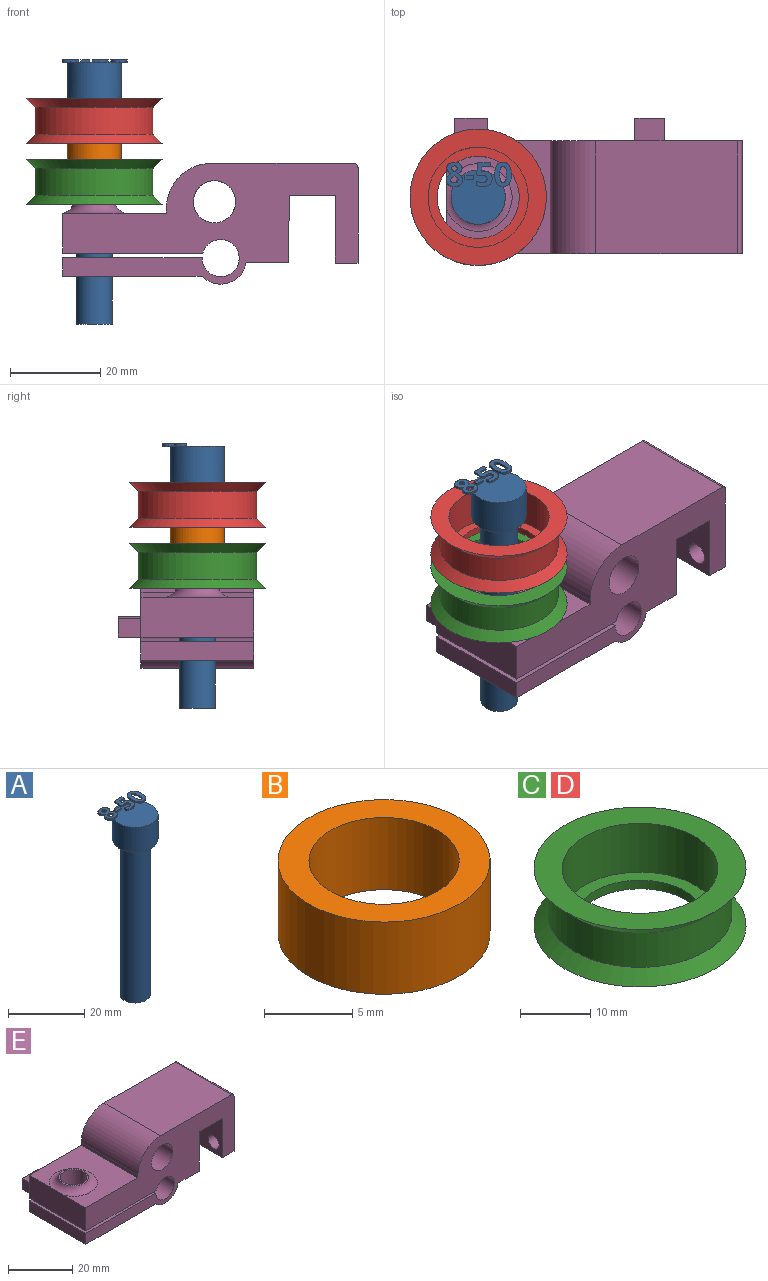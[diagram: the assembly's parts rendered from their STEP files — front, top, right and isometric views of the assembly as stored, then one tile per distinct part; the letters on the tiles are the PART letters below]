
ASSEMBLY  parts=5 mates=4
PART A: 86 faces, bbox 14.5x13.7x58.5 mm
  f0: plane 12x12mm, normal (0,0,1), area 99.4mm2, adj f5,f22,f23,f24,f25,f26,f40,f41
  f1: plane 1x0.26mm, normal (0,0,1), area 0.1mm2, adj f5,f46,f47,f48,f49
  f2: plane 0.85x0.68mm, normal (0,0,1), area 0.2mm2, adj f5,f29,f30,f31
  f3: cylinder r=4mm len=50mm, axis (0,0,-1), area 1256.6mm2, adj f4,f6
  f4: plane 8x8mm, normal (0,0,-1), area 50.3mm2, adj f3
  f5: cylinder r=6mm len=12mm, axis (0,0,-1), area 301.6mm2, adj f0,f1,f2,f6,f39,f45,f67,f85
  f6: plane 12x12mm, normal (0,0,-1), area 62.8mm2, adj f3,f5
  f7: extruded ~0.5x0.46mm, area 0.2mm2, adj f8,f37,f38,f39
  f8: extruded ~0.5x0.46mm, area 0.2mm2, adj f7,f9,f38,f39
  f9: extruded ~0.5x0.39mm, area 0.2mm2, adj f8,f10,f38,f39
  f10: extruded ~0.5x0.4mm, area 0.2mm2, adj f9,f11,f38,f39
  f11: extruded ~0.5x0.49mm, area 0.3mm2, adj f10,f12,f38,f39
  f12: extruded ~0.5x0.5mm, area 0.3mm2, adj f11,f13,f38,f39
  f13: extruded ~0.5x0.39mm, area 0.2mm2, adj f12,f37,f38,f39
  f14: extruded ~1.22x0.5mm, area 0.6mm2, adj f15,f35,f38,f39
  f15: extruded ~1.22x0.5mm, area 0.6mm2, adj f14,f16,f38,f39
  f16: extruded ~0.91x0.5mm, area 0.5mm2, adj f15,f17,f38,f39
  f17: extruded ~0.71x0.5mm, area 0.4mm2, adj f16,f18,f38,f39
  f18: extruded ~0.65x0.61mm, area 0.4mm2, adj f17,f19,f38,f39
  f19: extruded ~0.77x0.62mm, area 0.5mm2, adj f18,f20,f38,f39
  f20: extruded ~0.8x0.5mm, area 0.4mm2, adj f19,f21,f38,f39
  f21: extruded ~1.04x0.5mm, area 0.6mm2, adj f20,f22,f38,f39
  f22: extruded ~1.36x0.5mm, area 0.7mm2, adj f0,f21,f23,f38,f39
  f23: extruded ~1.33x0.5mm, area 0.7mm2, adj f0,f22,f24,f38
  f24: extruded ~1.04x0.51mm, area 0.6mm2, adj f0,f23,f25,f38
  f25: extruded ~0.75x0.5mm, area 0.4mm2, adj f0,f24,f26,f38
  f26: extruded ~0.85x0.66mm, area 0.5mm2, adj f0,f25,f27,f38,f39
  f27: extruded ~0.72x0.56mm, area 0.5mm2, adj f26,f28,f38,f39
  f28: extruded ~0.72x0.5mm, area 0.4mm2, adj f27,f35,f38,f39
  f29: extruded ~0.5x0.45mm, area 0.3mm2, adj f2,f30,f36,f38,f39
  f30: extruded ~0.5x0.47mm, area 0.3mm2, adj f2,f29,f31,f38
  f31: extruded ~0.62x0.5mm, area 0.3mm2, adj f2,f30,f32,f38,f39
  f32: extruded ~0.59x0.5mm, area 0.3mm2, adj f31,f33,f38,f39
  f33: extruded ~0.5x0.48mm, area 0.3mm2, adj f32,f34,f38,f39
  f34: extruded ~0.89x0.77mm, area 0.6mm2, adj f33,f36,f38,f39
  f35: extruded ~0.93x0.5mm, area 0.5mm2, adj f14,f28,f38,f39
  f36: extruded ~0.66x0.5mm, area 0.4mm2, adj f29,f34,f38,f39
  f37: extruded ~0.5x0.39mm, area 0.2mm2, adj f7,f13,f38,f39
  f38: plane 5.4x3.69mm, normal (0,0,1), area 12.7mm2, adj f7,f8,f9,f10,f11,f12,f13,f14
  f39: plane 5.4x3.53mm, normal (0,0,-1), area 10.2mm2, adj f5,f7,f8,f9,f10,f11,f12,f13
  f40: plane 0.9x0.5mm, normal (-1,0,0), area 0.4mm2, adj f0,f41,f43,f44
  f41: plane 1.93x0.5mm, normal (0,-1,0), area 1mm2, adj f0,f40,f42,f44
  f42: plane 0.9x0.5mm, normal (1,0,0), area 0.4mm2, adj f0,f41,f43,f44
  f43: plane 1.93x0.5mm, normal (0,1,0), area 1mm2, adj f0,f40,f42,f44
  f44: plane 1.93x0.9mm, normal (0,0,1), area 1.7mm2, adj f40,f41,f42,f43
  f45: plane 0.76x0.31mm, normal (0,0,-1), area 0mm2, adj f5,f46
  f46: extruded ~1.21x0.5mm, area 0.7mm2, adj f0,f1,f45,f47,f65,f66
  f47: extruded ~0.54x0.5mm, area 0.3mm2, adj f1,f46,f48,f66
  f48: plane 0.5x0.13mm, normal (-0.2,0.98,0), area 0.1mm2, adj f1,f47,f49,f66
  f49: plane 1.03x0.5mm, normal (1,-0.09,0), area 0.5mm2, adj f1,f48,f50,f66,f67
  f50: plane 1.88x0.5mm, normal (0,-1,0), area 0.9mm2, adj f49,f51,f66,f67
  f51: plane 0.94x0.5mm, normal (1,0,0), area 0.5mm2, adj f50,f52,f66,f67
  f52: plane 2.85x0.5mm, normal (0,1,0), area 1.4mm2, adj f51,f53,f66,f67
  f53: plane 2.68x0.5mm, normal (-1,0.07,0), area 1.3mm2, adj f0,f52,f54,f66,f67
  f54: plane 0.5x0.44mm, normal (-0.47,-0.88,0), area 0.3mm2, adj f0,f53,f55,f66
  f55: extruded ~0.5x0.37mm, area 0.2mm2, adj f0,f54,f56,f66
  f56: extruded ~0.5x0.42mm, area 0.2mm2, adj f0,f55,f57,f66
  f57: extruded ~1.05x0.8mm, area 0.8mm2, adj f0,f56,f58,f66
  f58: extruded ~1.02x0.83mm, area 0.8mm2, adj f0,f57,f59,f66
  f59: extruded ~0.72x0.5mm, area 0.4mm2, adj f0,f58,f60,f66
  f60: extruded ~0.66x0.5mm, area 0.4mm2, adj f0,f59,f61,f66
  f61: plane 0.96x0.5mm, normal (-1,0,0), area 0.5mm2, adj f0,f60,f62,f66
  f62: extruded ~1.42x0.5mm, area 0.7mm2, adj f0,f61,f63,f66
  f63: extruded ~1.55x0.5mm, area 0.8mm2, adj f0,f62,f64,f66
  f64: extruded ~1.36x0.54mm, area 0.8mm2, adj f0,f63,f65,f66
  f65: extruded ~1.17x0.5mm, area 0.6mm2, adj f0,f46,f64,f66
  f66: plane 5.33x3.51mm, normal (0,0,1), area 10.9mm2, adj f46,f47,f48,f49,f50,f51,f52,f53
  f67: plane 2.97x1.71mm, normal (0,0,-1), area 3.5mm2, adj f5,f49,f50,f51,f52,f53
  f68: extruded ~1.39x0.5mm, area 0.7mm2, adj f69,f83,f84,f85
  f69: extruded ~1.39x0.5mm, area 0.7mm2, adj f68,f70,f84,f85
  f70: extruded ~0.56x0.5mm, area 0.4mm2, adj f69,f71,f84,f85
  f71: extruded ~0.56x0.5mm, area 0.4mm2, adj f70,f72,f84,f85
  f72: extruded ~1.39x0.5mm, area 0.7mm2, adj f71,f73,f84,f85
  f73: extruded ~1.38x0.5mm, area 0.7mm2, adj f72,f74,f84,f85
  f74: extruded ~0.56x0.5mm, area 0.4mm2, adj f73,f83,f84,f85
  f75: extruded ~2.04x0.5mm, area 1.1mm2, adj f76,f82,f84,f85
  f76: extruded ~2.02x0.5mm, area 1.1mm2, adj f75,f77,f84,f85
  f77: extruded ~1.38x0.69mm, area 0.8mm2, adj f76,f78,f84,f85
  f78: extruded ~1.38x0.66mm, area 0.8mm2, adj f77,f79,f84,f85
  f79: extruded ~2.05x0.5mm, area 1.1mm2, adj f78,f80,f84,f85
  f80: extruded ~2.02x0.5mm, area 1mm2, adj f0,f79,f81,f84,f85
  f81: extruded ~1.37x0.68mm, area 0.8mm2, adj f0,f80,f82,f84
  f82: extruded ~1.39x0.66mm, area 0.8mm2, adj f0,f75,f81,f84,f85
  f83: extruded ~0.56x0.5mm, area 0.4mm2, adj f68,f74,f84,f85
  f84: plane 5.41x3.68mm, normal (0,0,1), area 12.1mm2, adj f68,f69,f70,f71,f72,f73,f74,f75
  f85: plane 5.41x3.68mm, normal (0,0,-1), area 10.3mm2, adj f5,f68,f69,f70,f71,f72,f73,f74
PART B: 4 faces, bbox 12x12x5 mm
  f0: cylinder r=4.25mm len=8.5mm, axis (0,0,-1), area 133.5mm2, adj f2,f3
  f1: cylinder r=6mm len=12mm, axis (0,0,-1), area 188.5mm2, adj f2,f3
  f2: plane 12x12mm, normal (0,0,1), area 56.4mm2, adj f0,f1
  f3: plane 12x12mm, normal (0,0,-1), area 56.4mm2, adj f0,f1
PART C: 8 faces, bbox 30.2x30.2x10 mm
  f0: plane 30.2x30.2mm, normal (0,0,1), area 329.2mm2, adj f1,f7
  f1: cylinder r=11.1mm len=22.2mm, axis (0,0,-1), area 592.8mm2, adj f0,f2
  f2: plane 22.2x22.2mm, normal (0,0,1), area 126.9mm2, adj f1,f3
  f3: cylinder r=9.1mm len=18.2mm, axis (0,0,-1), area 85.8mm2, adj f2,f4
  f4: plane 30.2x30.2mm, normal (0,0,-1), area 456.2mm2, adj f3,f5
  f5: cone r=13.1mm half-angle=45deg, axis (0,0,-1), area 250.6mm2, adj f4,f6
  f6: cylinder r=13.1mm len=26.2mm, axis (0,0,-1), area 493.9mm2, adj f5,f7
  f7: cone r=15.1mm half-angle=45deg, axis (0,0,1), area 250.6mm2, adj f0,f6
PART D: same geometry as C
PART E: 36 faces, bbox 68.9x30x26.7 mm
  f0: plane 25x4.12mm, normal (-1,0,0), area 103mm2, adj f3,f13,f14,f18
  f1: cylinder r=4.17mm len=8.35mm, axis (0,0,1), area 108.1mm2, adj f3,f18
  f2: plane 25x9.34mm, normal (0,0,-1), area 233.4mm2, adj f12,f13,f14,f16
  f3: plane 30.88x25mm, normal (0,0,-1), area 717.2mm2, adj f0,f1,f13,f14,f16
  f4: plane 25x8.82mm, normal (-1,0,0), area 219.6mm2, adj f5,f13,f14,f19,f23
  f5: plane 25x23mm, normal (0,0,1), area 400mm2, adj f4,f6,f13,f14,f23
  f6: plane 25x1.1mm, normal (-1,0,0), area 27.5mm2, adj f5,f13,f14,f24
  f7: plane 31.42x25mm, normal (0,0,1), area 785.6mm2, adj f13,f14,f24,f26
  f8: plane 25x21.09mm, normal (1,0,0), area 493.5mm2, adj f9,f13,f14,f21,f22,f26
  f9: plane 25x5mm, normal (0,0,-1), area 125mm2, adj f8,f10,f13,f14
  f10: plane 25x15mm, normal (-1,0,0), area 341.3mm2, adj f9,f11,f13,f14,f21,f22
  f11: plane 25x10.2mm, normal (0,0,-1), area 255mm2, adj f10,f12,f13,f14
  f12: plane 25x14.91mm, normal (1,0,-0.01), area 372.8mm2, adj f2,f11,f13,f14
  f13: plane 65.42x26.75mm, normal (0,-1,0), area 986.8mm2, adj f0,f2,f3,f4,f5,f6,f7,f8
  f14: plane 65.42x26.75mm, normal (0,1,0), area 926.8mm2, adj f0,f2,f3,f4,f5,f6,f7,f8
  f15: cylinder r=4.17mm len=10.78mm, axis (0,0,1), area 282.8mm2, adj f19,f20
  f16: cylinder r=5.75mm len=25mm, axis (0,-1,0), area 315.9mm2, adj f2,f3,f13,f14
  f17: cylinder r=4.1mm len=25mm, axis (0,-1,0), area 618.7mm2, adj f13,f14,f18,f19
  f18: plane 30.91x25mm, normal (0,0,1), area 718.1mm2, adj f0,f1,f13,f14,f17
  f19: plane 31.07x30mm, normal (0,0,-1), area 758.4mm2, adj f4,f13,f14,f15,f17,f28,f29,f30
  f20: plane 9.35x9.35mm, normal (0,0,1), area 13.9mm2, adj f15,f23
  f21: cylinder r=2.43mm len=5mm, axis (1,0,0), area 76.2mm2, adj f8,f10
  f22: cylinder r=2.2mm len=5mm, axis (1,0,0), area 69.1mm2, adj f8,f10
  f23: torus R=7.5mm, axis (0,0,-1), area 134.6mm2, adj f4,f5,f20
  f24: cylinder r=10mm len=25mm, axis (0,-1,0), area 392.7mm2, adj f6,f7,f13,f14
  f25: cylinder r=4.68mm len=25mm, axis (0,-1,0), area 735.2mm2, adj f13,f14
  f26: cylinder r=1mm len=25mm, axis (0,-1,0), area 39.3mm2, adj f7,f8,f13,f14
  f27: plane 7.3x5mm, normal (0,0,1), area 36.5mm2, adj f14,f28,f29,f30
  f28: plane 5x4.12mm, normal (-1,0,0), area 20.6mm2, adj f14,f19,f27,f30
  f29: plane 5x4.12mm, normal (1,0,0), area 20.6mm2, adj f14,f19,f27,f30
  f30: plane 7.3x4.12mm, normal (0,1,0), area 30.1mm2, adj f19,f27,f28,f29
  f31: plane 6.63x5mm, normal (0,0,1), area 33.2mm2, adj f14,f32,f34,f35
  f32: plane 5x4.5mm, normal (-1,0,0), area 22.5mm2, adj f14,f31,f33,f35
  f33: plane 6.63x5mm, normal (0,0,-1), area 33.2mm2, adj f14,f32,f34,f35
  f34: plane 5x4.5mm, normal (1,0,0), area 22.5mm2, adj f14,f31,f33,f35
  f35: plane 6.63x4.5mm, normal (0,1,0), area 29.9mm2, adj f31,f32,f33,f34
PLACE A t=(-103.78,-12.5,-13.6)mm
PLACE B rot(axis=(1,0,0),180deg) t=(-103.78,-12.5,26.4)mm
PLACE C t=(-103.78,-12.5,18.1)mm
PLACE D t=(-103.78,-12.5,31.6)mm
PLACE E at identity
MATE fastened A.f3 <-> D.f1  axis (0,0,-1) through (-103.78,-12.5,36.4)mm
MATE fastened B.f0 <-> C.f1  axis (0,0,1) through (-103.78,-12.5,21.4)mm
MATE fastened C.f1 <-> E.f1  axis (0,0,-1) through (-103.78,-12.5,12.9)mm
MATE fastened D.f1 <-> B.f0  axis (0,0,-1) through (-103.78,-12.5,26.4)mm
